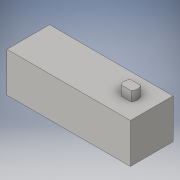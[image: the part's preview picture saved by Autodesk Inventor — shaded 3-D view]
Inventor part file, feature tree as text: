
AUTODESK INVENTOR PART (.ipt)
format: ipt  version: 2016 (Build 200138000, 138)  size: 97,792 bytes
history: native  units: in
note: dims shown in document units (in); Inventor stores cm internally (conversion verified against a paired STEP export)
features: extrude x2, sketch x2
ambient origin geometry x8: Origin, YZ Plane, XZ Plane, XY Plane, X Axis, Y Axis, Z Axis, Center Point
bodies: Solid1 (feature_tree)
feature tree (4):
  extrude  "Extrusion1"  Depth=0.83in
  extrude  "Extrusion2"  Depth=0.2in
  sketch  "Sketch1"  dims[d0=2.575in d1=0.83in]
  sketch  "Sketch2"  dims[d2=0.89in d3=0.0in d4=0.435in d5=0.21in d9=0.2in d10=0.0in]
